FCSTD DOCUMENT  (FreeCAD 0.16RUnknown)
Label: shape
License: All rights reserved
LicenseURL: http://en.wikipedia.org/wiki/All_rights_reserved
objects: Sketcher::SketchObject×1, Drawing::FeatureViewPart×1, Drawing::FeaturePage×1
note: 1 computed .brp shape members not serialized (recipe doc carries the construction recipe); baked Part::Feature solids carry a one-line shape summary decoded from their .brp

FEATURE [Sketcher::SketchObject] Sketch001
  Placement = pos=(0,0,0) rot=(0.57735,0.57735,0.57735;2.0944rad)
  sketch-geometry (34):
    g0: LineSegment StartX=-45 StartY=-102.426 StartZ=0 EndX=45 EndY=-102.426 EndZ=0
    g1: LineSegment StartX=-45 StartY=-102.426 StartZ=0 EndX=-38.7868 EndY=-87.4264 EndZ=0
    g2: LineSegment StartX=-38.7868 StartY=-87.4264 StartZ=0 EndX=38.7868 EndY=-87.4264 EndZ=0
    g3: LineSegment StartX=38.7868 StartY=-87.4264 StartZ=0 EndX=45 EndY=-102.426 EndZ=0
    g4: LineSegment StartX=87.4264 StartY=38.7868 StartZ=0 EndX=87.4264 EndY=-38.7868 EndZ=0
    g5: LineSegment StartX=87.4264 StartY=-38.7868 StartZ=0 EndX=102.426 EndY=-45 EndZ=0
    g6: LineSegment StartX=102.426 StartY=-45 StartZ=0 EndX=102.426 EndY=45 EndZ=0
    g7: LineSegment StartX=102.426 StartY=45 StartZ=0 EndX=87.4264 EndY=38.7868 EndZ=0
    g8: LineSegment StartX=-87.4264 StartY=38.7868 StartZ=0 EndX=-87.4264 EndY=-38.7868 EndZ=0
    g9: LineSegment StartX=-87.4264 StartY=-38.7868 StartZ=0 EndX=-102.426 EndY=-45 EndZ=0
    g10: LineSegment StartX=-102.426 StartY=-45 StartZ=0 EndX=-102.426 EndY=45 EndZ=0
    g11: LineSegment StartX=-102.426 StartY=45 StartZ=0 EndX=-87.4264 EndY=38.7868 EndZ=0
    g12: LineSegment StartX=45 StartY=102.426 StartZ=0 EndX=38.7868 EndY=87.4264 EndZ=0
    g13: LineSegment StartX=38.7868 StartY=87.4264 StartZ=0 EndX=-38.7868 EndY=87.4264 EndZ=0
    g14: LineSegment StartX=-38.7868 StartY=87.4264 StartZ=0 EndX=-45 EndY=102.426 EndZ=0
    g15: LineSegment StartX=-45 StartY=102.426 StartZ=0 EndX=45 EndY=102.426 EndZ=0
    g16: LineSegment StartX=-45 StartY=102.426 StartZ=0 EndX=-102.426 EndY=45 EndZ=0
    g17: LineSegment StartX=-38.7868 StartY=87.4264 StartZ=0 EndX=-87.4264 EndY=38.7868 EndZ=0
    g18: LineSegment StartX=-45 StartY=-102.426 StartZ=0 EndX=-102.426 EndY=-45 EndZ=0
    g19: LineSegment StartX=102.426 StartY=-45 StartZ=0 EndX=45 EndY=-102.426 EndZ=0
    g20: LineSegment StartX=45 StartY=102.426 StartZ=0 EndX=102.426 EndY=45 EndZ=0
    g21: LineSegment StartX=-87.4264 StartY=-38.7868 StartZ=0 EndX=-38.7868 EndY=-87.4264 EndZ=0
    g22: LineSegment StartX=87.4264 StartY=-38.7868 StartZ=0 EndX=38.7868 EndY=-87.4264 EndZ=0
    g23: LineSegment StartX=87.4264 StartY=38.7868 StartZ=0 EndX=38.7868 EndY=87.4264 EndZ=0
    g24: LineSegment [constr] StartX=38.7868 StartY=87.4264 StartZ=0 EndX=38.7868 EndY=-87.4264 EndZ=0
    g25: LineSegment [constr] StartX=87.4264 StartY=-38.7868 StartZ=0 EndX=-87.4264 EndY=-38.7868 EndZ=0
    g26: LineSegment [constr] StartX=102.426 StartY=-45 StartZ=0 EndX=87.4264 EndY=-45 EndZ=0
    g27: LineSegment [constr] StartX=87.4264 StartY=-45 StartZ=0 EndX=87.4264 EndY=-38.7868 EndZ=0
    g28: LineSegment [constr] StartX=45 StartY=-102.426 StartZ=0 EndX=45 EndY=-87.4264 EndZ=0
    g29: LineSegment [constr] StartX=45 StartY=-87.4264 StartZ=0 EndX=38.7868 EndY=-87.4264 EndZ=0
    g30: LineSegment [constr] StartX=45 StartY=-87.4264 StartZ=0 EndX=87.4264 EndY=-45 EndZ=0
    g31: LineSegment [constr] StartX=87.4264 StartY=38.7868 StartZ=0 EndX=98.033 EndY=49.3934 EndZ=0
    g32: LineSegment [constr] StartX=38.7868 StartY=87.4264 StartZ=0 EndX=38.7868 EndY=102.426 EndZ=0
    g33: LineSegment [constr] StartX=-38.7868 StartY=87.4264 StartZ=0 EndX=-49.3934 EndY=98.033 EndZ=0
  constraints (87):
    c: Coincident(g0,g1)
    c: Coincident(g1,g2)
    c: Coincident(g2,g3)
    c: Coincident(g5,g6)
    c: Coincident(g6,g7)
    c: Coincident(g7,g4)
    c: Vertical(g8)
    c: Coincident(g8,g9)
    c: Coincident(g9,g10)
    c: Vertical(g10)
    c: Coincident(g10,g11)
    c: Coincident(g11,g8)
    c: Coincident(g12,g13)
    c: Horizontal(g13)
    c: Coincident(g13,g14)
    c: Coincident(g14,g15)
    c: Coincident(g15,g12)
    c: Symmetric(g4,g8,g-1)
    c: Symmetric(g8,g4,g-1)
    c: Symmetric(g2,g13,g-1)
    c: Symmetric(g1,g12,g-1)
    c: Horizontal(g15)
    c: Coincident(g3,g0)
    c: Symmetric(g12,g0,g-1)
    c: Symmetric(g14,g0,g-1)
    c: Symmetric(g5,g10,g-1)
    c: Symmetric(g6,g9,g-1)
    c: Coincident(g5,g4)
    c: DistanceX(g5,g5) = 15
    c: Coincident(g16,g14)
    c: Coincident(g16,g10)
    c: Coincident(g18,g0)
    c: Coincident(g19,g5)
    c: Coincident(g19,g0)
    c: Coincident(g20,g12)
    c: Coincident(g20,g6)
    c: Coincident(g17,g13)
    c: Coincident(g17,g8)
    c: Coincident(g18,g9)
    c: Coincident(g21,g8)
    c: Coincident(g22,g4)
    c: Coincident(g22,g2)
    c: Coincident(g23,g4)
    c: Coincident(g23,g12)
    c: Coincident(g21,g1)
    c: Parallel(g16,g17)
    c: Parallel(g20,g23)
    c: Equal(g6,g0)
    c: DistanceY(g10,g10) = 90
    c: Coincident(g24,g12)
    c: Coincident(g24,g2)
    c: Vertical(g24)
    c: Coincident(g25,g4)
    c: Coincident(g25,g8)
    c: Horizontal(g25)
    c: Equal(g24,g25)
    c: Coincident(g26,g5)
    c: Horizontal(g26)
    c: Coincident(g27,g4)
    c: Vertical(g27)
    c: Coincident(g28,g0)
    c: Vertical(g28)
    c: Coincident(g29,g28)
    c: Coincident(g29,g2)
    c: Horizontal(g29)
    c: Coincident(g30,g28)
    c: Coincident(g30,g27)
    c: Coincident(g26,g27)
    c: Distance(g30) = 60
    c: Coincident(g31,g4)
    c: PointOnObject(g31,g20)
    c: Perpendicular(g31,g20)
    c: Coincident(g32,g12)
    c: PointOnObject(g32,g15)
    c: Vertical(g32)
    c: Coincident(g33,g13)
    c: PointOnObject(g33,g16)
    c: Perpendicular(g33,g16)
    c: Equal(g26,g31)
    c: Equal(g31,g32)
    c: Equal(g32,g33)
    c: DistanceY(g8,g8) = 77.5736
    c: Distance(g18) = 81.2132
    c: Distance(g23) = 68.7868
    c: Angle(g10,g11) = 1.1781
    c: Angle(g11,g16) = 1.1781
    c: DistanceY(g0,g12) = 204.853
FEATURE [Drawing::FeatureViewPart] View
  Direction = (1,0,0)
  HiddenWidth = 0.15
  LineWidth = 0.35
  Rotation = 0
  ShowHiddenLines = false
  ShowSmoothLines = false
  Source = -> Sketch001
  Tolerance = 0.05
  ViewResult = <g id="View"\n   transform="rotate(0,150,105) translate(150,105) scale(1,1)"\n  >\n<g   stroke="rgb(0, 0, 0)"\n   stroke-width="0.35"\n   stroke-linecap="butt"\n   stroke-linejoin="miter"\n   fill="none"\n   transform="scale(1,-1)"\n  >\n<path id= "1" d=" M -102.426 45 L -102.426 -45 " />\n<path id= "2" d=" M -45 -102.426 L -102.426 -45 " />\n<path id= "3" d=" M -38.7868 -87.4264 L -45 -102.426 " />\n<path id= "4" d=" M -45 -102.426 L 45 -102.426 " />\n<path id= "5" d=" M 45 -102.426 L 38.7868 -87.4264 " />\n<path id= "6" d=" M 38.7868 -87.4264 L 87.4264 -38.7868 " />\n<path id= "7" d=" M 102.426 -45 L 87.4264 -38.7868 " />\n<path id= "8" d=" M 87.4264 -38.7868 L 87.4264 38.7868 " />\n<path id= "9" d=" M 87.4264 38.7868 L 38.7868 87.4264 " />\n<path id= "10" d=" M 45 102.426 L 38.7868 87.4264 " />\n<path id= "11" d=" M 38.7868 87.4264 L -38.7868 87.4264 " />\n<path id= "12" d=" M -45 102.426 L 45 102.426 " />\n<path id= "13" d=" M 102.426 45 L 45 102.426 " />\n<path id= "14" d=" M 87.4264 38.7868 L 102.426 45 " />\n<path id= "15" d=" M 102.426 45 L 102.426 -45 " />\n<path id= "16" d=" M 102.426 -45 L 45 -102.426 " />\n<path id= "17" d=" M 38.7868 -87.4264 L -38.7868 -87.4264 " />\n<path id= "18" d=" M -38.7868 -87.4264 L -87.4264 -38.7868 " />\n<path id= "19" d=" M -87.4264 -38.7868 L -102.426 -45 " />\n<path id= "20" d=" M -87.4264 38.7868 L -87.4264 -38.7868 " />\n<path id= "21" d=" M -102.426 45 L -87.4264 38.7868 " />\n<path id= "22" d=" M -102.426 45 L -45 102.426 " />\n<path id= "23" d=" M -38.7868 87.4264 L -45 102.426 " />\n<path id= "24" d=" M -38.7868 87.4264 L -87.4264 38.7868 " />\n</g>\n</g>
  Visible = true
  X = 150
  Y = 105
FEATURE [Drawing::FeaturePage] Page003  label="drawing"
  Group = -> [View]
